# Revit family: Donna 17_ Pendant
name_source: partatom
category: Lighting Fixtures
revit_build: Autodesk Revit 2017 (Build: 20190508_0315(x64)
units: mm (PartAtom-declared; Revit-internal decimal feet)

## family parameters
Cut with Voids When Loaded = No
Host = Face
Light Source = Yes
Part Type = Normal
Room Calculation Point = No
Round Connector Dimension = Use Diameter
Shared = No

## types (1)
- Donna 17_ Pendant
    Canopy Width = 6"
    Color Filter = 16777215
    Cost = 599 $
    Default Elevation = 0"
    Description = Part of a captivating collection of mid-century-inspired light fixtures, the Donna 17" Pendant encapsulates the flash and fervor of vintage Italian design. A mushroom-shaped shade with generously-scaled uplight perforations creates a uniquely dramatic silhouette. Featuring a double socket and white-painted shade interior for soft, glowing illumination, the high-end detailing of the Donna series may be appreciated from every angle.Crafted from hand-polished, heavy gauge aluminum, the Donna series is available in three visually-striking finishes, each hand-applied by specialty finishing shops local to our factory. High-shine Polished Aluminum is polished to a stunning mirror-finish and completed with a protective clear coat. The rich Gold Anodized and Black Anodized finishes are achieved through anodizing - an environmentally friendly electrochemical process that bonds the finish to the material for a beautiful and durable effect. Assembled in our Portland, Ore. factory using ethically-sourced domestic and global components. A Schoolhouse Original.
    Dimming Lamp Color Temperature Shift = <None>
    Height = 15"
    Light Source Symbol Length = 8 1/2"
    Max Wattage = 60 W
    Primary Finishes = Polished Aluminum, Gold Annodized, Black
    Product Material = Schoolhouse_Aluminum
    Spot Beam Angle = 30.00°
    Spot Field Angle = 90.00°
    Tilt Angle = 60.00°
    URL = https://www.schoolhouse.com
    Voltage = 120 /220V
    Width = 17"

## geometry (parser evidence)
native form markers: Sweep x3
no freeform markers — native parametric forms only
